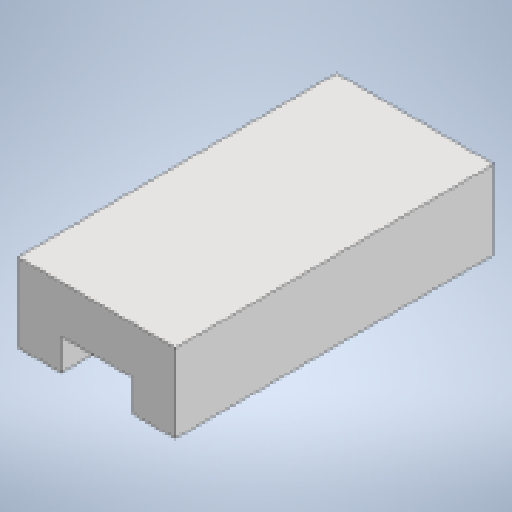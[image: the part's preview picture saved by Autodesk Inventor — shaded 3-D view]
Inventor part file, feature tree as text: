
AUTODESK INVENTOR PART (.ipt)
format: ipt  version: 2025.3 (Build 293356030, 356C)  size: 120,832 bytes
history: native  units: mm
features: extrude x1, sketch x1
ambient origin geometry x8: Origin, YZ Plane, XZ Plane, XY Plane, X Axis, Y Axis, Z Axis, Center Point
bodies: Solid1 (feature_tree)
feature tree (2):
  extrude  "Extrusion1"  Depth=4.0mm
  sketch  "Sketch1"  dims[d0=9.0mm d1=4.0mm d2=10.0mm d3=20.0mm d4=40.5mm d5=0.0mm]
